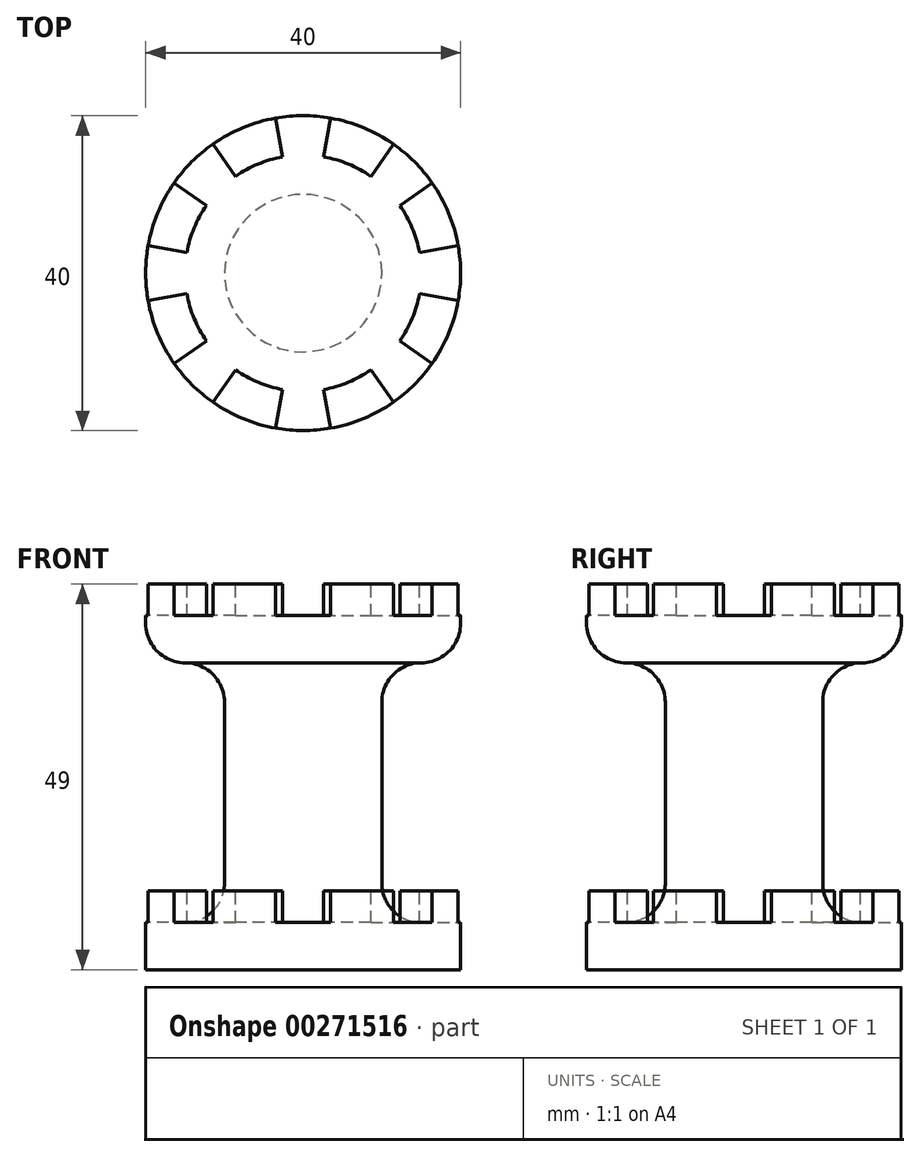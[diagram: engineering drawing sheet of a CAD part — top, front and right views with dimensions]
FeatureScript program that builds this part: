
annotation { "Feature Type Name" : "Feature", "Feature Type Description" : "" }
export const myFeature = defineFeature(function(context is Context, id is Id, definition is map)
    precondition{}
    {
        {
            var Q0;
            Q0=qCreatedBy(makeId("Front.planeOp"),FACE);
            var sketch = newSketch(context, id + "F0", { "sketchPlane" : qUnion([Q0])});
            skLineSegment(sketch, "E0.right", {"start": v(-10, 6) * mm, "end": v(-10, 39) * mm});
            skLineSegment(sketch, "E1.top", {"start": v(-10, 6) * mm, "end": v(-15, 6) * mm});
            skLineSegment(sketch, "E2.bottom", {"start": v(-10, 39) * mm, "end": v(-20, 39) * mm});
            skLineSegment(sketch, "E2.top", {"start": v(-15, 49) * mm, "end": v(-20, 49) * mm});
            skLineSegment(sketch, "E2.right", {"start": v(-20, 39) * mm, "end": v(-20, 49) * mm});
            skLineSegment(sketch, "E3.top", {"start": v(0, 45) * mm, "end": v(-15, 45) * mm});
            skLineSegment(sketch, "E3.right", {"start": v(-15, 49) * mm, "end": v(-15, 45) * mm});
            skLineSegment(sketch, "E4", {"start": v(0, 0) * mm, "end": v(0, 45) * mm});
            skLineSegment(sketch, "E5", {"start": v(0, 0) * mm, "end": v(-20, 0) * mm});
            skLineSegment(sketch, "E6.top", {"start": v(-20, 10) * mm, "end": v(-15, 10) * mm});
            skLineSegment(sketch, "E6.right", {"start": v(-15, 6) * mm, "end": v(-15, 10) * mm});
            skLineSegment(sketch, "E7", {"start": v(-20, 0) * mm, "end": v(-20, 10) * mm});
            skSolve(sketch);
        }
        {
            var Q0;
            Q0 = qSketchRegion(id + "F0", true);
            var Q1;
            Q1=sQuery(id+"F0.wireOp",EDGE,"E4");
            revolve(context, id + "F1", {"entities" : qUnion([Q0]), "axis" : qUnion([Q1]), "revolveType" : RevolveType.FULL});
        }
        {
            var Q0;
            Q0=makeQuery(id+"F1.opRevolve","SWEPT_FACE",FACE,{"disambiguationData":[OSD([sQuery(id+"F0.wireOp",EDGE,"E2.top")])]});
            var sketch = newSketch(context, id + "F2", { "sketchPlane" : qUnion([Q0])});
            skLineSegment(sketch, "E8", {"start": v(2.6, 14.77) * mm, "end": v(3.64, 20.62) * mm});
            skLineSegment(sketch, "E9", {"start": v(-2.6, 14.77) * mm, "end": v(-3.64, 20.62) * mm});
            skArc(sketch, "E10", {"start": v(2.6, 14.77) * mm, "mid": v(0, 15) * mm, "end": v(-2.6, 14.77) * mm});
            skArc(sketch, "E11", {"start": v(3.64, 20.62) * mm, "mid": v(0, 20.93) * mm, "end": v(-3.64, 20.62) * mm});
            skLineSegment(sketch, "E12.1.0", {"start": v(-8.6, 12.29) * mm, "end": v(-12, 17.15) * mm});
            skArc(sketch, "E12.1.1", {"start": v(-8.6, 12.29) * mm, "mid": v(-10.6, 10.6) * mm, "end": v(-12.29, 8.6) * mm});
            skLineSegment(sketch, "E12.1.2", {"start": v(-12.29, 8.6) * mm, "end": v(-17.15, 12) * mm});
            skArc(sketch, "E12.1.3", {"start": v(-12, 17.15) * mm, "mid": v(-14.8, 14.8) * mm, "end": v(-17.15, 12) * mm});
            skLineSegment(sketch, "E12.2.0", {"start": v(-14.77, 2.6) * mm, "end": v(-20.62, 3.64) * mm});
            skArc(sketch, "E12.2.1", {"start": v(-14.77, 2.6) * mm, "mid": v(-15, 0) * mm, "end": v(-14.77, -2.6) * mm});
            skLineSegment(sketch, "E12.2.2", {"start": v(-14.77, -2.6) * mm, "end": v(-20.62, -3.64) * mm});
            skArc(sketch, "E12.2.3", {"start": v(-20.62, 3.64) * mm, "mid": v(-20.93, 0) * mm, "end": v(-20.62, -3.64) * mm});
            skLineSegment(sketch, "E12.3.0", {"start": v(-12.29, -8.6) * mm, "end": v(-17.15, -12) * mm});
            skArc(sketch, "E12.3.1", {"start": v(-12.29, -8.6) * mm, "mid": v(-10.6, -10.6) * mm, "end": v(-8.6, -12.29) * mm});
            skLineSegment(sketch, "E12.3.2", {"start": v(-8.6, -12.29) * mm, "end": v(-12, -17.15) * mm});
            skArc(sketch, "E12.3.3", {"start": v(-17.15, -12) * mm, "mid": v(-14.8, -14.8) * mm, "end": v(-12, -17.15) * mm});
            skLineSegment(sketch, "E12.4.0", {"start": v(-2.6, -14.77) * mm, "end": v(-3.64, -20.62) * mm});
            skArc(sketch, "E12.4.1", {"start": v(-2.6, -14.77) * mm, "mid": v(0, -15) * mm, "end": v(2.6, -14.77) * mm});
            skLineSegment(sketch, "E12.4.2", {"start": v(2.6, -14.77) * mm, "end": v(3.64, -20.62) * mm});
            skArc(sketch, "E12.4.3", {"start": v(-3.64, -20.62) * mm, "mid": v(0, -20.93) * mm, "end": v(3.64, -20.62) * mm});
            skLineSegment(sketch, "E12.5.0", {"start": v(8.6, -12.29) * mm, "end": v(12, -17.15) * mm});
            skArc(sketch, "E12.5.1", {"start": v(8.6, -12.29) * mm, "mid": v(10.6, -10.6) * mm, "end": v(12.29, -8.6) * mm});
            skLineSegment(sketch, "E12.5.2", {"start": v(12.29, -8.6) * mm, "end": v(17.15, -12) * mm});
            skArc(sketch, "E12.5.3", {"start": v(12, -17.15) * mm, "mid": v(14.8, -14.8) * mm, "end": v(17.15, -12) * mm});
            skLineSegment(sketch, "E12.6.0", {"start": v(14.77, -2.6) * mm, "end": v(20.62, -3.64) * mm});
            skArc(sketch, "E12.6.1", {"start": v(14.77, -2.6) * mm, "mid": v(15, 0) * mm, "end": v(14.77, 2.6) * mm});
            skLineSegment(sketch, "E12.6.2", {"start": v(14.77, 2.6) * mm, "end": v(20.62, 3.64) * mm});
            skArc(sketch, "E12.6.3", {"start": v(20.62, -3.64) * mm, "mid": v(20.93, 0) * mm, "end": v(20.62, 3.64) * mm});
            skLineSegment(sketch, "E12.7.0", {"start": v(12.29, 8.6) * mm, "end": v(17.15, 12) * mm});
            skArc(sketch, "E12.7.1", {"start": v(12.29, 8.6) * mm, "mid": v(10.6, 10.6) * mm, "end": v(8.6, 12.29) * mm});
            skLineSegment(sketch, "E12.7.2", {"start": v(8.6, 12.29) * mm, "end": v(12, 17.15) * mm});
            skArc(sketch, "E12.7.3", {"start": v(17.15, 12) * mm, "mid": v(14.8, 14.8) * mm, "end": v(12, 17.15) * mm});
            skSolve(sketch);
        }
        {
            var Q0;
            Q0 = qSketchRegion(id + "F2", true);
            extrude(context, id + "F3", {"entities" : qUnion([Q0]), "operationType" : NewBodyOperationType.REMOVE, "oppositeDirection" : true, "depth" : 43 * mm});
        }
        {
            var Q0;
            {var subQ0=sQuery(id+"F2.wireOp",EDGE,"E12.4.1");Q0=makeQuery(id+"F2.imprint","IMPRINT",FACE,{"disambiguationData":[TD([[makeQuery(id+"F2.imprint","IMPRINT",EDGE,{"derivedFrom":subQ0}),1.0]])]});}
            var Q1;
            {var subQ0=sQuery(id+"F2.wireOp",EDGE,"E12.5.1");Q1=makeQuery(id+"F2.imprint","IMPRINT",FACE,{"disambiguationData":[TD([[makeQuery(id+"F2.imprint","IMPRINT",EDGE,{"derivedFrom":subQ0}),1.0]])]});}
            var Q2;
            {var subQ0=sQuery(id+"F2.wireOp",EDGE,"E12.6.1");Q2=makeQuery(id+"F2.imprint","IMPRINT",FACE,{"disambiguationData":[TD([[makeQuery(id+"F2.imprint","IMPRINT",EDGE,{"derivedFrom":subQ0}),1.0]])]});}
            var Q3;
            {var subQ0=sQuery(id+"F2.wireOp",EDGE,"E12.7.1");Q3=makeQuery(id+"F2.imprint","IMPRINT",FACE,{"disambiguationData":[TD([[makeQuery(id+"F2.imprint","IMPRINT",EDGE,{"derivedFrom":subQ0}),1.0]])]});}
            var Q4;
            {var subQ0=sQuery(id+"F2.wireOp",EDGE,"E10");Q4=makeQuery(id+"F2.imprint","IMPRINT",FACE,{"disambiguationData":[TD([[makeQuery(id+"F2.imprint","IMPRINT",EDGE,{"derivedFrom":subQ0}),1.0]])]});}
            var Q5;
            {var subQ0=sQuery(id+"F2.wireOp",EDGE,"E12.1.1");Q5=makeQuery(id+"F2.imprint","IMPRINT",FACE,{"disambiguationData":[TD([[makeQuery(id+"F2.imprint","IMPRINT",EDGE,{"derivedFrom":subQ0}),1.0]])]});}
            var Q6;
            {var subQ0=sQuery(id+"F2.wireOp",EDGE,"E12.2.1");Q6=makeQuery(id+"F2.imprint","IMPRINT",FACE,{"disambiguationData":[TD([[makeQuery(id+"F2.imprint","IMPRINT",EDGE,{"derivedFrom":subQ0}),1.0]])]});}
            var Q7;
            {var subQ0=sQuery(id+"F2.wireOp",EDGE,"E12.3.1");Q7=makeQuery(id+"F2.imprint","IMPRINT",FACE,{"disambiguationData":[TD([[makeQuery(id+"F2.imprint","IMPRINT",EDGE,{"derivedFrom":subQ0}),1.0]])]});}
            extrude(context, id + "F4", {"entities" : qUnion([Q0, Q1, Q2, Q3, Q4, Q5, Q6, Q7]), "operationType" : NewBodyOperationType.ADD, "oppositeDirection" : true, "depth" : 10 * mm});
        }
        {
            var Q0;
            {var subQ0=sQuery(id+"F2.wireOp",EDGE,"E12.5.1");Q0=makeQuery(id+"F2.imprint","IMPRINT",FACE,{"disambiguationData":[TD([[makeQuery(id+"F2.imprint","IMPRINT",EDGE,{"derivedFrom":subQ0}),1.0]])]});}
            var Q1;
            {var subQ0=sQuery(id+"F2.wireOp",EDGE,"E12.6.1");Q1=makeQuery(id+"F2.imprint","IMPRINT",FACE,{"disambiguationData":[TD([[makeQuery(id+"F2.imprint","IMPRINT",EDGE,{"derivedFrom":subQ0}),1.0]])]});}
            var Q2;
            {var subQ0=sQuery(id+"F2.wireOp",EDGE,"E12.7.1");Q2=makeQuery(id+"F2.imprint","IMPRINT",FACE,{"disambiguationData":[TD([[makeQuery(id+"F2.imprint","IMPRINT",EDGE,{"derivedFrom":subQ0}),1.0]])]});}
            var Q3;
            {var subQ0=sQuery(id+"F2.wireOp",EDGE,"E10");Q3=makeQuery(id+"F2.imprint","IMPRINT",FACE,{"disambiguationData":[TD([[makeQuery(id+"F2.imprint","IMPRINT",EDGE,{"derivedFrom":subQ0}),1.0]])]});}
            var Q4;
            {var subQ0=sQuery(id+"F2.wireOp",EDGE,"E12.1.1");Q4=makeQuery(id+"F2.imprint","IMPRINT",FACE,{"disambiguationData":[TD([[makeQuery(id+"F2.imprint","IMPRINT",EDGE,{"derivedFrom":subQ0}),1.0]])]});}
            var Q5;
            {var subQ0=sQuery(id+"F2.wireOp",EDGE,"E12.2.1");Q5=makeQuery(id+"F2.imprint","IMPRINT",FACE,{"disambiguationData":[TD([[makeQuery(id+"F2.imprint","IMPRINT",EDGE,{"derivedFrom":subQ0}),1.0]])]});}
            var Q6;
            {var subQ0=sQuery(id+"F2.wireOp",EDGE,"E12.3.1");Q6=makeQuery(id+"F2.imprint","IMPRINT",FACE,{"disambiguationData":[TD([[makeQuery(id+"F2.imprint","IMPRINT",EDGE,{"derivedFrom":subQ0}),1.0]])]});}
            var Q7;
            {var subQ0=sQuery(id+"F2.wireOp",EDGE,"E12.4.1");Q7=makeQuery(id+"F2.imprint","IMPRINT",FACE,{"disambiguationData":[TD([[makeQuery(id+"F2.imprint","IMPRINT",EDGE,{"derivedFrom":subQ0}),1.0]])]});}
            extrude(context, id + "F5", {"entities" : qUnion([Q0, Q1, Q2, Q3, Q4, Q5, Q6, Q7]), "operationType" : NewBodyOperationType.REMOVE, "oppositeDirection" : true, "depth" : 4 * mm});
        }
        {
            var Q0;
            Q0=makeQuery(id+"F1.opRevolve","SWEPT_FACE",FACE,{"disambiguationData":[OSD([sQuery(id+"F0.wireOp",EDGE,"E0.right")])]});
            var Q1;
            {var subQ0=sQuery(id+"F0.wireOp",EDGE,"E2.right");var subQ1=sQuery(id+"F0.wireOp",EDGE,"E2.top");Q1=makeQuery(id+"F4.boolean.opBoolean","MERGE",FACE,{"derivedFrom":[makeQuery(id+"F1.opRevolve","SWEPT_FACE",FACE,{"disambiguationData":[OSD([sQuery(id+"F0.wireOp",EDGE,"E2.bottom")])]}),makeQuery(id+"F4.opExtrude","CAP_FACE",FACE,{"disambiguationData":[OSD([subQ1,subQ0,sQuery(id+"F2.wireOp",EDGE,"E8"),sQuery(id+"F2.wireOp",EDGE,"E9"),sQuery(id+"F2.wireOp",EDGE,"E10")])],"isStart":false}),makeQuery(id+"F4.opExtrude","CAP_FACE",FACE,{"disambiguationData":[OSD([subQ1,subQ0,sQuery(id+"F2.wireOp",EDGE,"E12.1.0"),sQuery(id+"F2.wireOp",EDGE,"E12.1.1"),sQuery(id+"F2.wireOp",EDGE,"E12.1.2")])],"isStart":false}),makeQuery(id+"F4.opExtrude","CAP_FACE",FACE,{"disambiguationData":[OSD([subQ1,subQ0,sQuery(id+"F2.wireOp",EDGE,"E12.2.0"),sQuery(id+"F2.wireOp",EDGE,"E12.2.1"),sQuery(id+"F2.wireOp",EDGE,"E12.2.2")])],"isStart":false}),makeQuery(id+"F4.opExtrude","CAP_FACE",FACE,{"disambiguationData":[OSD([subQ1,subQ0,sQuery(id+"F2.wireOp",EDGE,"E12.3.0"),sQuery(id+"F2.wireOp",EDGE,"E12.3.1"),sQuery(id+"F2.wireOp",EDGE,"E12.3.2")])],"isStart":false}),makeQuery(id+"F4.opExtrude","CAP_FACE",FACE,{"disambiguationData":[OSD([subQ1,subQ0,sQuery(id+"F2.wireOp",EDGE,"E12.4.0"),sQuery(id+"F2.wireOp",EDGE,"E12.4.1"),sQuery(id+"F2.wireOp",EDGE,"E12.4.2")])],"isStart":false}),makeQuery(id+"F4.opExtrude","CAP_FACE",FACE,{"disambiguationData":[OSD([subQ1,subQ0,sQuery(id+"F2.wireOp",EDGE,"E12.5.0"),sQuery(id+"F2.wireOp",EDGE,"E12.5.1"),sQuery(id+"F2.wireOp",EDGE,"E12.5.2")])],"isStart":false}),makeQuery(id+"F4.opExtrude","CAP_FACE",FACE,{"disambiguationData":[OSD([subQ1,subQ0,sQuery(id+"F2.wireOp",EDGE,"E12.6.0"),sQuery(id+"F2.wireOp",EDGE,"E12.6.1"),sQuery(id+"F2.wireOp",EDGE,"E12.6.2")])],"isStart":false}),makeQuery(id+"F4.opExtrude","CAP_FACE",FACE,{"disambiguationData":[OSD([subQ1,subQ0,sQuery(id+"F2.wireOp",EDGE,"E12.7.0"),sQuery(id+"F2.wireOp",EDGE,"E12.7.1"),sQuery(id+"F2.wireOp",EDGE,"E12.7.2")])],"isStart":false})]});}
            fillet(context, id + "F6", {"entities" : qUnion([Q0, Q1]), "radius" : 5 * mm, "tangentPropagation" : true, "allowEdgeOverflow" : false});
        }
    });
